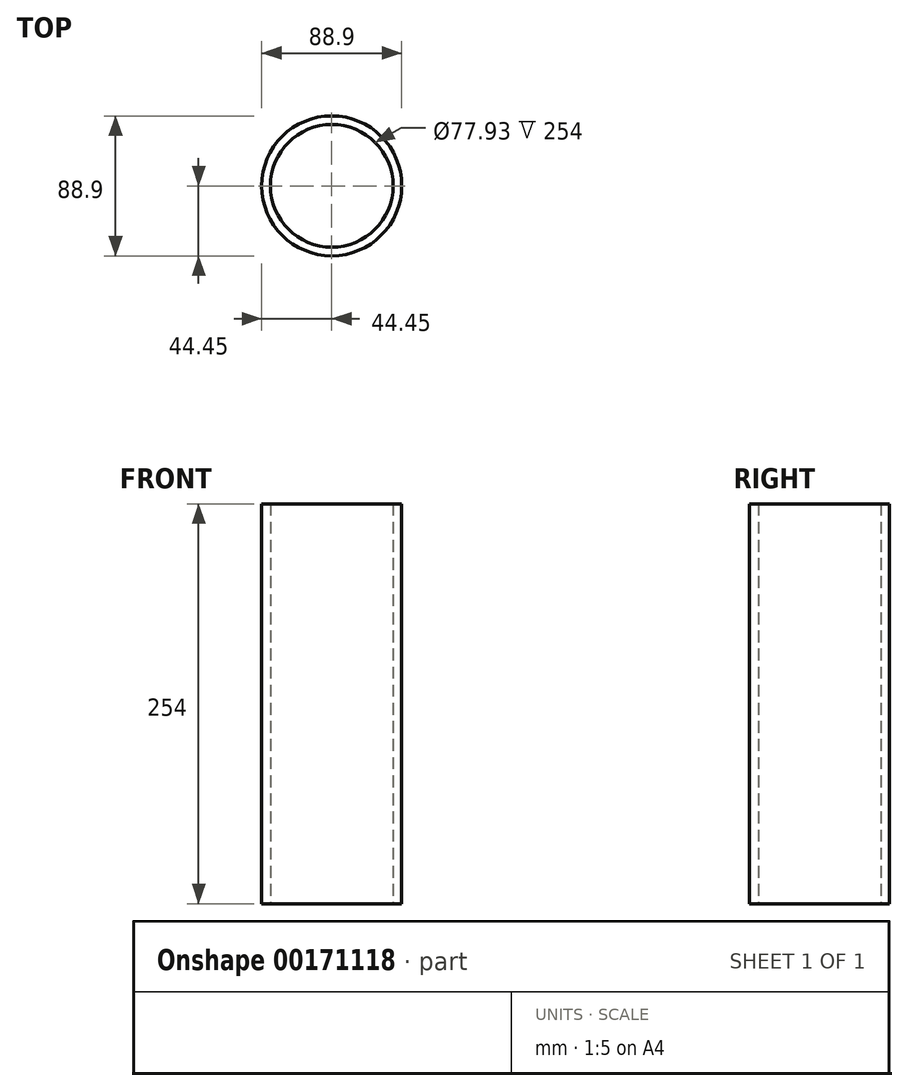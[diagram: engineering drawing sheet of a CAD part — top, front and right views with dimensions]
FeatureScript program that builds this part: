
annotation { "Feature Type Name" : "Feature", "Feature Type Description" : "" }
export const myFeature = defineFeature(function(context is Context, id is Id, definition is map)
    precondition{}
    {
        {
            var Q0;
            Q0=qCreatedBy(makeId("Top.planeOp"),FACE);
            var sketch = newSketch(context, id + "F0", { "sketchPlane" : qUnion([Q0])});
            skCircle(sketch, "E0", {"center": v(0, 0) * mm, "radius": 44.45 * mm});
            skCircle(sketch, "E1", {"center": v(0, 0) * mm, "radius": 38.96 * mm});
            skSolve(sketch);
        }
        {
            var Q0;
            Q0=makeQuery(id+"F0.imprint","IMPRINT",FACE,{"disambiguationData":[TD([[makeQuery(id+"F0.imprint","IMPRINT",EDGE,{"derivedFrom":sQuery(id+"F0.wireOp",EDGE,"E0")}),1.0]])]});
            extrude(context, id + "F1", {"entities" : qUnion([Q0]), "endBound" : BoundingType.SYMMETRIC, "depth" : 254 * mm});
        }
    });
